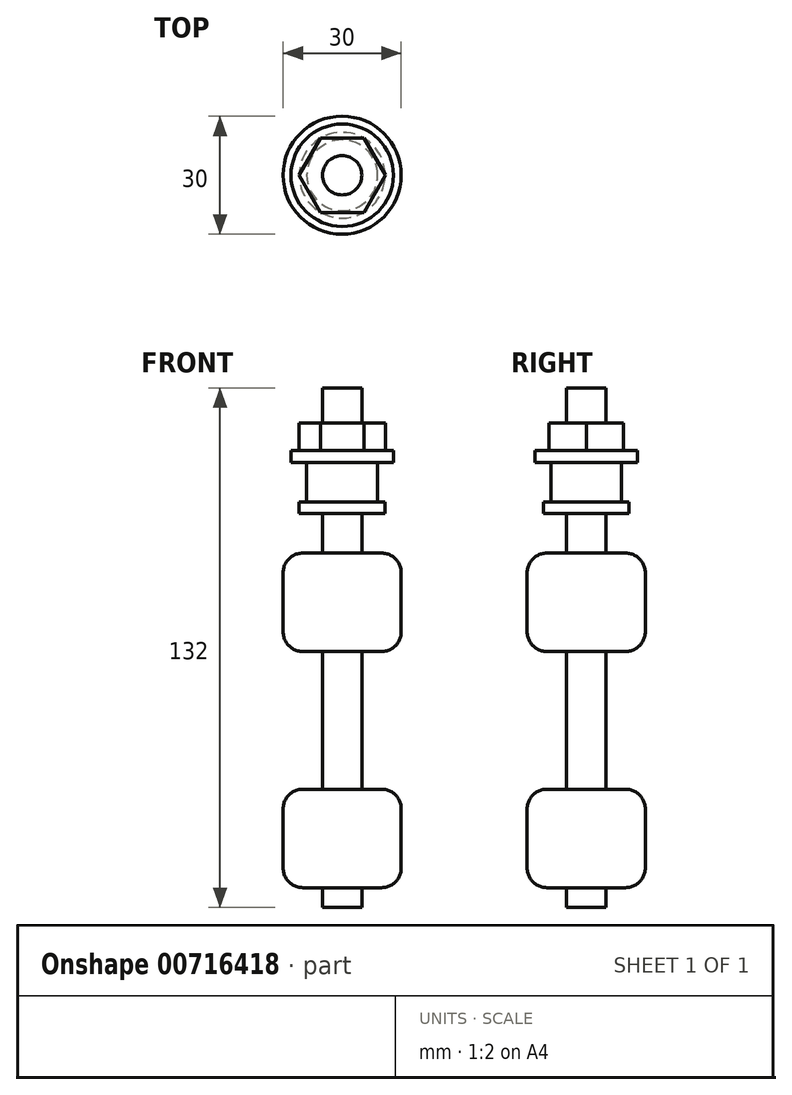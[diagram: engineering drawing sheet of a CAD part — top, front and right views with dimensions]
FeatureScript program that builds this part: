
annotation { "Feature Type Name" : "Feature", "Feature Type Description" : "" }
export const myFeature = defineFeature(function(context is Context, id is Id, definition is map)
    precondition{}
    {
        {
            var Q0;
            Q0=qCreatedBy(makeId("Top.planeOp"),FACE);
            var sketch = newSketch(context, id + "F0", { "sketchPlane" : qUnion([Q0])});
            skCircle(sketch, "E0", {"center": v(0, 0) * mm, "radius": 10.9 * mm});
            skSolve(sketch);
        }
        {
            var Q0;
            Q0=qSketchRegion(id+"F0",true);
            extrude(context, id + "F1", {"entities" : qUnion([Q0]), "depth" : 3 * mm, "offsetDistance" : 25 * mm});
        }
        {
            var Q0;
            Q0=makeQuery(id+"F1.opExtrude","CAP_FACE",FACE,{"disambiguationData":[OSD([sQuery(id+"F0.wireOp",EDGE,"E0")])],"isStart":false});
            var sketch = newSketch(context, id + "F2", { "sketchPlane" : qUnion([Q0])});
            skCircle(sketch, "E1", {"center": v(0, 0) * mm, "radius": 9 * mm});
            skSolve(sketch);
        }
        {
            var Q0;
            Q0=qSketchRegion(id+"F2",true);
            extrude(context, id + "F3", {"entities" : qUnion([Q0]), "operationType" : NewBodyOperationType.ADD, "depth" : 10 * mm, "offsetDistance" : 25 * mm});
        }
        {
            var Q0;
            Q0=makeQuery(id+"F3.opExtrude","CAP_FACE",FACE,{"disambiguationData":[OSD([sQuery(id+"F2.wireOp",EDGE,"E1")])],"isStart":false});
            var sketch = newSketch(context, id + "F4", { "sketchPlane" : qUnion([Q0])});
            skCircle(sketch, "E2", {"center": v(0, 0) * mm, "radius": 13 * mm});
            skSolve(sketch);
        }
        {
            var Q0;
            Q0=qSketchRegion(id+"F4",true);
            extrude(context, id + "F5", {"entities" : qUnion([Q0]), "operationType" : NewBodyOperationType.ADD, "depth" : 3 * mm, "offsetDistance" : 25 * mm});
        }
        {
            var Q0;
            Q0=makeQuery(id+"F5.opExtrude","CAP_FACE",FACE,{"disambiguationData":[OSD([sQuery(id+"F4.wireOp",EDGE,"E2")])],"isStart":false});
            var sketch = newSketch(context, id + "F6", { "sketchPlane" : qUnion([Q0])});
            skCircle(sketch, "E3.cCircle", {"center": v(0, 0) * mm, "radius": 9.5 * mm, "construction": true});
            skLineSegment(sketch, "E3.0", {"start": v(5.48, -9.5) * mm, "end": v(-5.48, -9.5) * mm});
            skLineSegment(sketch, "E3.1", {"start": v(-5.48, -9.5) * mm, "end": v(-10.97, 0) * mm});
            skLineSegment(sketch, "E3.2", {"start": v(-10.97, 0) * mm, "end": v(-5.48, 9.5) * mm});
            skLineSegment(sketch, "E3.3", {"start": v(-5.48, 9.5) * mm, "end": v(5.48, 9.5) * mm});
            skLineSegment(sketch, "E3.4", {"start": v(5.48, 9.5) * mm, "end": v(10.97, 0) * mm});
            skLineSegment(sketch, "E3.5", {"start": v(10.97, 0) * mm, "end": v(5.48, -9.5) * mm});
            skPoint(sketch, "E3.0.midPoint", {"position": v(0, -9.5) * mm});
            skSolve(sketch);
        }
        {
            var Q0;
            Q0=qSketchRegion(id+"F6",true);
            extrude(context, id + "F7", {"entities" : qUnion([Q0]), "operationType" : NewBodyOperationType.ADD, "depth" : 7 * mm, "offsetDistance" : 25 * mm});
        }
        {
            var Q0;
            Q0=makeQuery(id+"F7.opExtrude","CAP_FACE",FACE,{"disambiguationData":[OSD([sQuery(id+"F6.wireOp",EDGE,"E3.0"),sQuery(id+"F6.wireOp",EDGE,"E3.1"),sQuery(id+"F6.wireOp",EDGE,"E3.2"),sQuery(id+"F6.wireOp",EDGE,"E3.3"),sQuery(id+"F6.wireOp",EDGE,"E3.4"),sQuery(id+"F6.wireOp",EDGE,"E3.5")])],"isStart":false});
            var sketch = newSketch(context, id + "F8", { "sketchPlane" : qUnion([Q0])});
            skCircle(sketch, "E4", {"center": v(0, 0) * mm, "radius": 5 * mm});
            skSolve(sketch);
        }
        {
            var Q0;
            Q0=qSketchRegion(id+"F8",true);
            extrude(context, id + "F9", {"entities" : qUnion([Q0]), "operationType" : NewBodyOperationType.ADD, "depth" : 9 * mm, "offsetDistance" : 25 * mm});
        }
        {
            var Q0;
            Q0=makeQuery(id+"F1.opExtrude","CAP_FACE",FACE,{"disambiguationData":[OSD([sQuery(id+"F0.wireOp",EDGE,"E0")])],"isStart":true});
            var sketch = newSketch(context, id + "F10", { "sketchPlane" : qUnion([Q0])});
            skCircle(sketch, "E5", {"center": v(0, 0) * mm, "radius": 5 * mm});
            skSolve(sketch);
        }
        {
            var Q0;
            Q0=qSketchRegion(id+"F10",true);
            extrude(context, id + "F11", {"entities" : qUnion([Q0]), "operationType" : NewBodyOperationType.ADD, "depth" : 100 * mm, "offsetDistance" : 25 * mm});
        }
        {
            var Q0;
            Q0=makeQuery(id+"F11.opExtrude","CAP_FACE",FACE,{"disambiguationData":[OSD([sQuery(id+"F10.wireOp",EDGE,"E5")])],"isStart":false});
            cPlane(context, id + "F12", {"entities" : qUnion([Q0]), "cplaneType" : CPlaneType.OFFSET, "offset" : 5 * mm, "oppositeDirection" : true, "width" : 150 * mm, "height" : 150 * mm});
        }
        {
            var Q0;
            Q0=qCreatedBy(id+"F12.planeOp",FACE);
            var sketch = newSketch(context, id + "F13", { "sketchPlane" : qUnion([Q0])});
            skCircle(sketch, "E6", {"center": v(0, 0) * mm, "radius": 15 * mm});
            skSolve(sketch);
        }
        {
            var Q0;
            Q0 = qSketchRegion(id + "F13", true);
            extrude(context, id + "F14", {"entities" : qUnion([Q0]), "operationType" : NewBodyOperationType.ADD, "oppositeDirection" : true, "depth" : 25 * mm, "offsetDistance" : 25 * mm});
        }
        {
            var Q0;
            Q0=makeQuery(id+"F11.opExtrude","CAP_FACE",FACE,{"disambiguationData":[OSD([sQuery(id+"F10.wireOp",EDGE,"E5")])],"isStart":false});
            cPlane(context, id + "F15", {"entities" : qUnion([Q0]), "cplaneType" : CPlaneType.OFFSET, "offset" : 65 * mm, "oppositeDirection" : true, "width" : 150 * mm, "height" : 150 * mm});
        }
        {
            var Q0;
            Q0=qCreatedBy(id+"F15.planeOp",FACE);
            var sketch = newSketch(context, id + "F16", { "sketchPlane" : qUnion([Q0])});
            skCircle(sketch, "E7", {"center": v(0, 0) * mm, "radius": 15 * mm});
            skSolve(sketch);
        }
        {
            var Q0;
            Q0 = qSketchRegion(id + "F16", true);
            extrude(context, id + "F17", {"entities" : qUnion([Q0]), "operationType" : NewBodyOperationType.ADD, "oppositeDirection" : true, "depth" : 25 * mm, "offsetDistance" : 25 * mm});
        }
        {
            var Q0;
            Q0=makeQuery(id+"F14.opExtrude","CAP_EDGE",EDGE,{"disambiguationData":[OSD([sQuery(id+"F13.wireOp",EDGE,"E6")])],"isStart":false});
            var Q1;
            Q1=makeQuery(id+"F14.opExtrude","CAP_EDGE",EDGE,{"disambiguationData":[OSD([sQuery(id+"F13.wireOp",EDGE,"E6")])],"isStart":true});
            var Q2;
            Q2=makeQuery(id+"F17.opExtrude","CAP_EDGE",EDGE,{"disambiguationData":[OSD([sQuery(id+"F16.wireOp",EDGE,"E7")])],"isStart":false});
            var Q3;
            Q3=makeQuery(id+"F17.opExtrude","CAP_EDGE",EDGE,{"disambiguationData":[OSD([sQuery(id+"F16.wireOp",EDGE,"E7")])],"isStart":true});
            fillet(context, id + "F18", {"entities" : qUnion([Q0, Q1, Q2, Q3]), "radius" : 5 * mm, "tangentPropagation" : true, "allowEdgeOverflow" : false});
        }
    });
